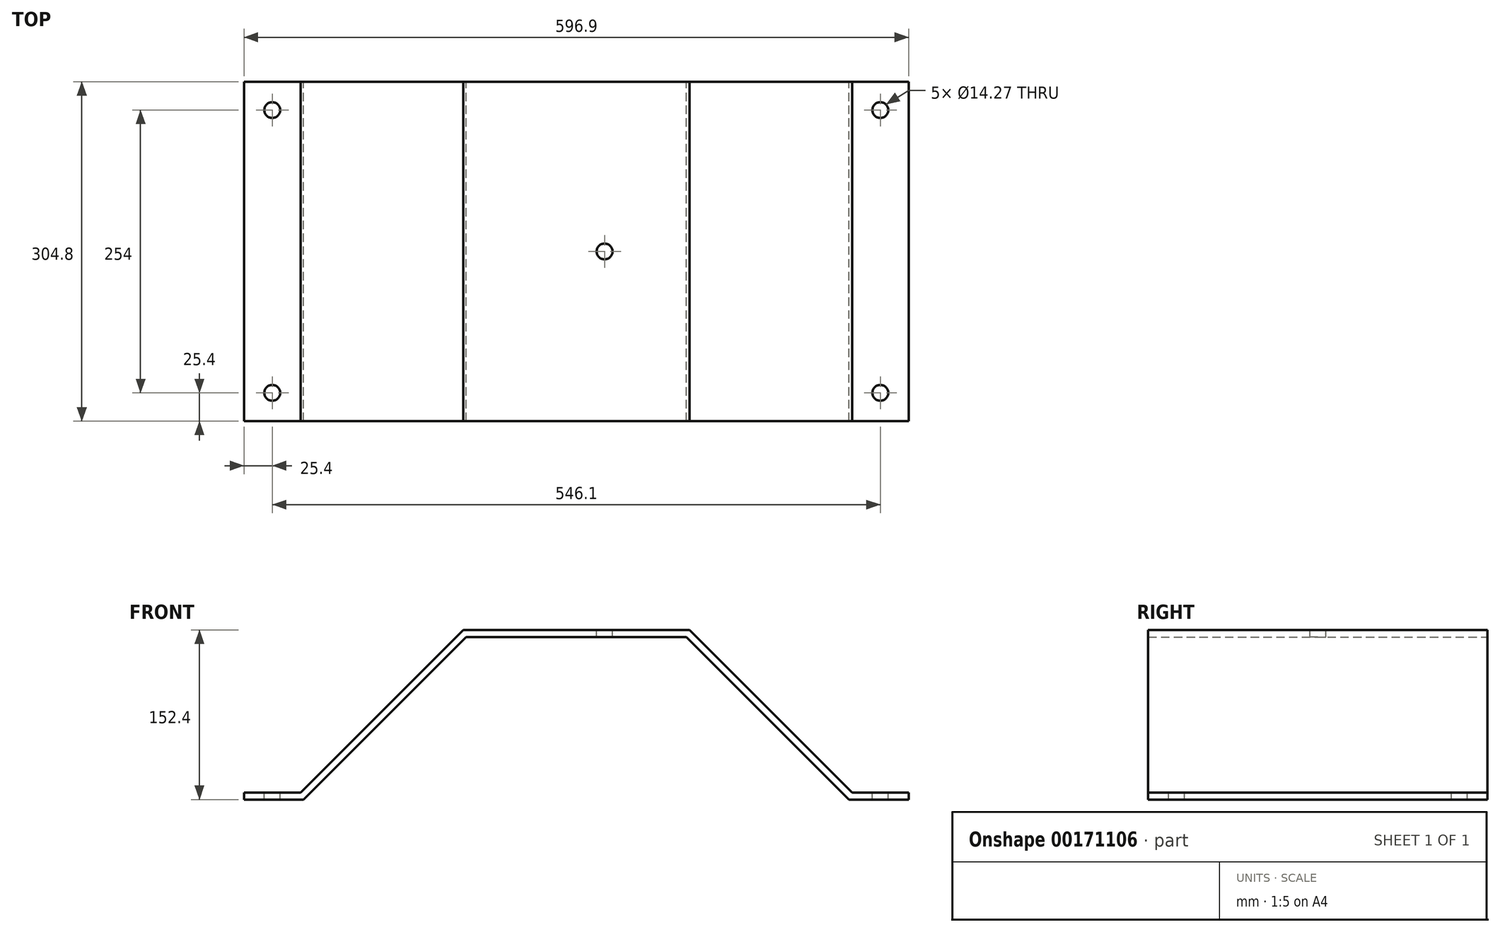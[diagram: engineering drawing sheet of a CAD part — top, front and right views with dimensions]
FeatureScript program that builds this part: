
annotation { "Feature Type Name" : "Feature", "Feature Type Description" : "" }
export const myFeature = defineFeature(function(context is Context, id is Id, definition is map)
    precondition{}
    {
        {
            var Q0;
            Q0=qCreatedBy(makeId("Front.planeOp"),FACE);
            var sketch = newSketch(context, id + "F0", { "sketchPlane" : qUnion([Q0])});
            skLineSegment(sketch, "E0", {"start": v(-298.45, -146.05) * mm, "end": v(-247.65, -146.05) * mm});
            skLineSegment(sketch, "E1", {"start": v(-247.65, -146.05) * mm, "end": v(-101.6, 0) * mm});
            skLineSegment(sketch, "E2", {"start": v(-101.6, 0) * mm, "end": v(101.6, 0) * mm});
            skLineSegment(sketch, "E3", {"start": v(101.6, 0) * mm, "end": v(247.65, -146.05) * mm});
            skLineSegment(sketch, "E4", {"start": v(247.65, -146.05) * mm, "end": v(298.45, -146.05) * mm});
            skLineSegment(sketch, "E5", {"start": v(298.45, -146.05) * mm, "end": v(298.45, -152.4) * mm});
            skLineSegment(sketch, "E6", {"start": v(298.45, -152.4) * mm, "end": v(245.02, -152.4) * mm});
            skLineSegment(sketch, "E7", {"start": v(245.02, -152.4) * mm, "end": v(98.97, -6.35) * mm});
            skLineSegment(sketch, "E8", {"start": v(98.97, -6.35) * mm, "end": v(-98.97, -6.35) * mm});
            skLineSegment(sketch, "E9", {"start": v(-98.97, -6.35) * mm, "end": v(-245.02, -152.4) * mm});
            skLineSegment(sketch, "E10", {"start": v(-245.02, -152.4) * mm, "end": v(-298.45, -152.4) * mm});
            skLineSegment(sketch, "E11", {"start": v(-298.45, -152.4) * mm, "end": v(-298.45, -146.05) * mm});
            skSolve(sketch);
        }
        {
            var Q0;
            Q0 = qSketchRegion(id + "F0", true);
            extrude(context, id + "F1", {"entities" : qUnion([Q0]), "endBound" : BoundingType.SYMMETRIC, "depth" : 304.8 * mm});
        }
        {
            var Q0;
            Q0=makeQuery(id+"F1.opExtrude","SWEPT_FACE",FACE,{"disambiguationData":[OSD([sQuery(id+"F0.wireOp",EDGE,"E0")])]});
            var sketch = newSketch(context, id + "F2", { "sketchPlane" : qUnion([Q0])});
            skCircle(sketch, "E12", {"center": v(-273.05, 127) * mm, "radius": 7.14 * mm});
            skLineSegment(sketch, "E13", {"start": v(0, 153.87) * mm, "end": v(0, -153.07) * mm});
            skLineSegment(sketch, "E14", {"start": v(-298.45, 0) * mm, "end": v(298.26, 0) * mm});
            skPoint(sketch, "E14.endSnap0", {"position": v(-298.45, 0) * mm});
            skCircle(sketch, "E15.MirrorC", {"center": v(-273.05, -127) * mm, "radius": 7.14 * mm});
            skCircle(sketch, "E16.MirrorC", {"center": v(273.05, 127) * mm, "radius": 7.14 * mm});
            skCircle(sketch, "E17.MirrorC", {"center": v(273.05, -127) * mm, "radius": 7.14 * mm});
            skSolve(sketch);
        }
        {
            var Q0;
            Q0 = qSketchRegion(id + "F2", true);
            extrude(context, id + "F3", {"entities" : qUnion([Q0]), "operationType" : NewBodyOperationType.REMOVE, "endBound" : BoundingType.THROUGH_ALL, "oppositeDirection" : true, "depth" : 25.4 * mm});
        }
        {
            var Q0;
            Q0=makeQuery(id+"F1.opExtrude","SWEPT_FACE",FACE,{"disambiguationData":[OSD([sQuery(id+"F0.wireOp",EDGE,"E2")])]});
            var sketch = newSketch(context, id + "F4", { "sketchPlane" : qUnion([Q0])});
            skLineSegment(sketch, "E18", {"start": v(-101.6, 0) * mm, "end": v(101.6, 0) * mm});
            skCircle(sketch, "E19", {"center": v(25.4, 0) * mm, "radius": 7.14 * mm});
            skSolve(sketch);
        }
        {
            var Q0;
            Q0 = qSketchRegion(id + "F4", true);
            extrude(context, id + "F5", {"entities" : qUnion([Q0]), "operationType" : NewBodyOperationType.REMOVE, "endBound" : BoundingType.THROUGH_ALL, "oppositeDirection" : true, "depth" : 25.4 * mm});
        }
    });
